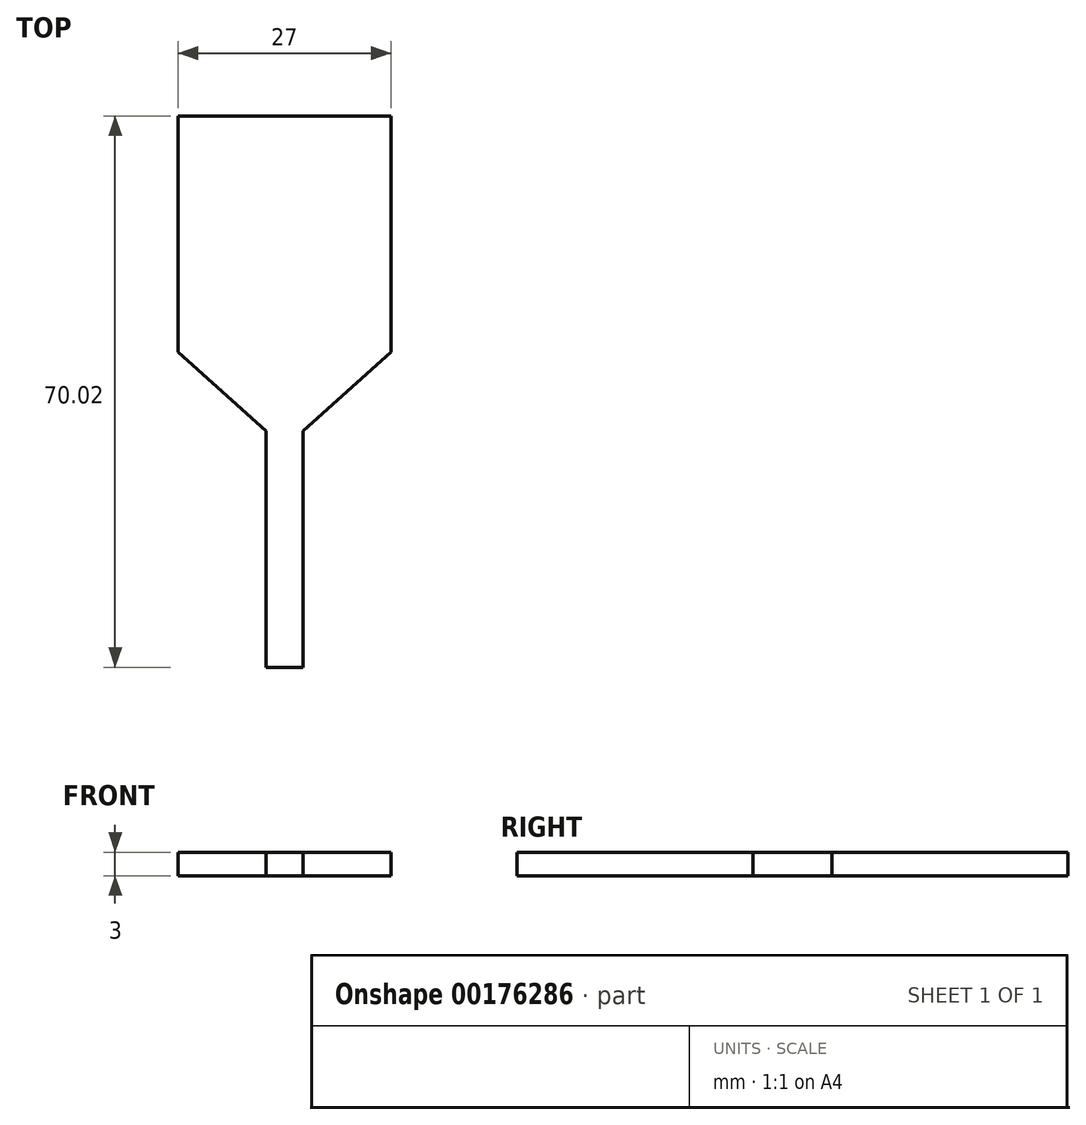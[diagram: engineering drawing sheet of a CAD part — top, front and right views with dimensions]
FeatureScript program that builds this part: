
annotation { "Feature Type Name" : "Feature", "Feature Type Description" : "" }
export const myFeature = defineFeature(function(context is Context, id is Id, definition is map)
    precondition{}
    {
        {
            var Q0;
            Q0=qCreatedBy(makeId("Top.planeOp"),FACE);
            var sketch = newSketch(context, id + "F0", { "sketchPlane" : qUnion([Q0])});
            skLineSegment(sketch, "E0", {"start": v(13.5, 3.34) * mm, "end": v(13.5, -26.66) * mm});
            skLineSegment(sketch, "E1", {"start": v(13.5, -26.66) * mm, "end": v(2.33, -36.68) * mm});
            skLineSegment(sketch, "E2", {"start": v(2.33, -36.68) * mm, "end": v(2.33, -66.68) * mm});
            skLineSegment(sketch, "E3.MirrorCS", {"start": v(-13.5, 3.34) * mm, "end": v(-13.5, -26.66) * mm});
            skLineSegment(sketch, "E4.MirrorCS", {"start": v(-13.5, -26.66) * mm, "end": v(-2.33, -36.68) * mm});
            skLineSegment(sketch, "E5.MirrorCS", {"start": v(-2.33, -36.68) * mm, "end": v(-2.33, -66.68) * mm});
            skLineSegment(sketch, "E6", {"start": v(-13.5, 3.34) * mm, "end": v(13.5, 3.34) * mm});
            skLineSegment(sketch, "E7", {"start": v(-2.33, -66.68) * mm, "end": v(2.33, -66.68) * mm});
            skSolve(sketch);
        }
        {
            var Q0;
            Q0=makeQuery(id+"F0.imprint","IMPRINT",FACE,{"disambiguationData":[TD([[makeQuery(id+"F0.imprint","IMPRINT",EDGE,{"derivedFrom":sQuery(id+"F0.wireOp",EDGE,"E0")}),-1.0]])]});
            extrude(context, id + "F1", {"entities" : qUnion([Q0]), "depth" : 3 * mm});
        }
    });
